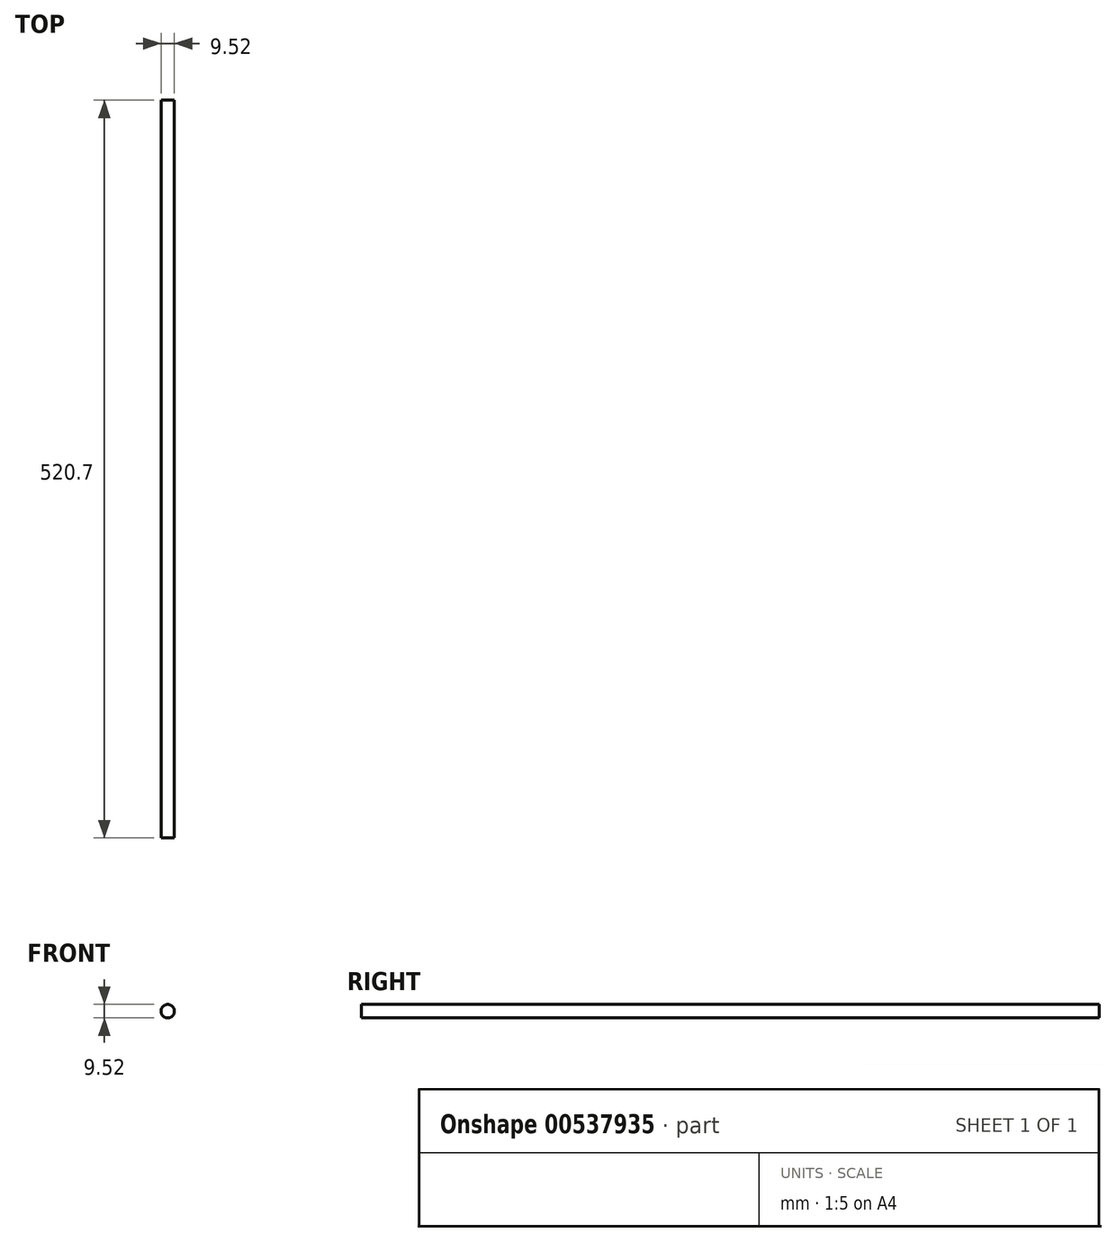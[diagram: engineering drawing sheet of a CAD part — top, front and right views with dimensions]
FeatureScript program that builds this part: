
annotation { "Feature Type Name" : "Feature", "Feature Type Description" : "" }
export const myFeature = defineFeature(function(context is Context, id is Id, definition is map)
    precondition{}
    {
        {
            var Q0;
            Q0=qCreatedBy(makeId("Front.planeOp"),FACE);
            var sketch = newSketch(context, id + "F0", { "sketchPlane" : qUnion([Q0])});
            skCircle(sketch, "E0", {"center": v(0, 0) * mm, "radius": 4.76 * mm});
            skSolve(sketch);
        }
        {
            var Q0;
            Q0 = qSketchRegion(id + "F0", true);
            extrude(context, id + "F1", {"entities" : qUnion([Q0]), "oppositeDirection" : true, "depth" : 520.7 * mm, "offsetDistance" : 25.4 * mm});
        }
    });
